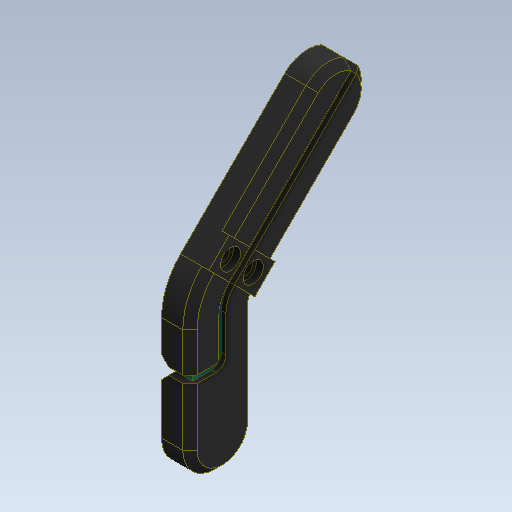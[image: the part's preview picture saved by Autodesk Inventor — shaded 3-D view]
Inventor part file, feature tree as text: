
AUTODESK INVENTOR PART (.ipt)
format: ipt  version: 2020 (Build 240168000, 168)  size: 396,288 bytes
history: native  units: in
note: dims shown in document units (in); Inventor stores cm internally (conversion verified against a paired STEP export)
features: sketch x30, other x7, plane x4
ambient origin geometry x8: Origin, YZ Plane, XZ Plane, XY Plane, X Axis, Y Axis, Z Axis, Center Point
bodies: Solid2 (feature_tree), Solid3 (feature_tree), Solid1 (feature_tree), Solid4 (feature_tree)
feature tree (41):
  other  "PatellaTop.ipt"
  other  "Solid1::PatellaTop.ipt"
  other  "Solid4::PatellaTop.ipt"
  other  "Solid5::PatellaTop.ipt"
  other  "Solid2::PatellaTop.ipt"
  other  "Solid3::PatellaTop.ipt"
  other  "TaggingFeature1"
  sketch  "Sketch1"  dims[d0=0.3937in]
  sketch  "Sketch2"
  sketch  "Sketch3"
  sketch  "Sketch4"
  sketch  "Sketch5"
  sketch  "Sketch12"
  sketch  "Sketch14"
  sketch  "Sketch15"
  sketch  "Sketch16"
  sketch  "Sketch17"
  sketch  "Sketch19"
  sketch  "Sketch22"
  sketch  "Sketch23"
  sketch  "Sketch24"
  sketch  "Sketch25"
  sketch  "Sketch26"
  sketch  "Sketch27"
  sketch  "Sketch28"
  sketch  "Sketch29"
  sketch  "Sketch30"
  sketch  "Sketch31"
  sketch  "Sketch32"
  sketch  "Sketch33"
  sketch  "Sketch39"
  sketch  "Sketch40"
  sketch  "Sketch44"
  sketch  "Sketch45"
  sketch  "Sketch46"
  sketch  "Sketch48"
  sketch  "Sketch49"
  plane  "Work Plane1"
  plane  "Work Plane2"
  plane  "Work Plane3"
  plane  "Work Plane4"
